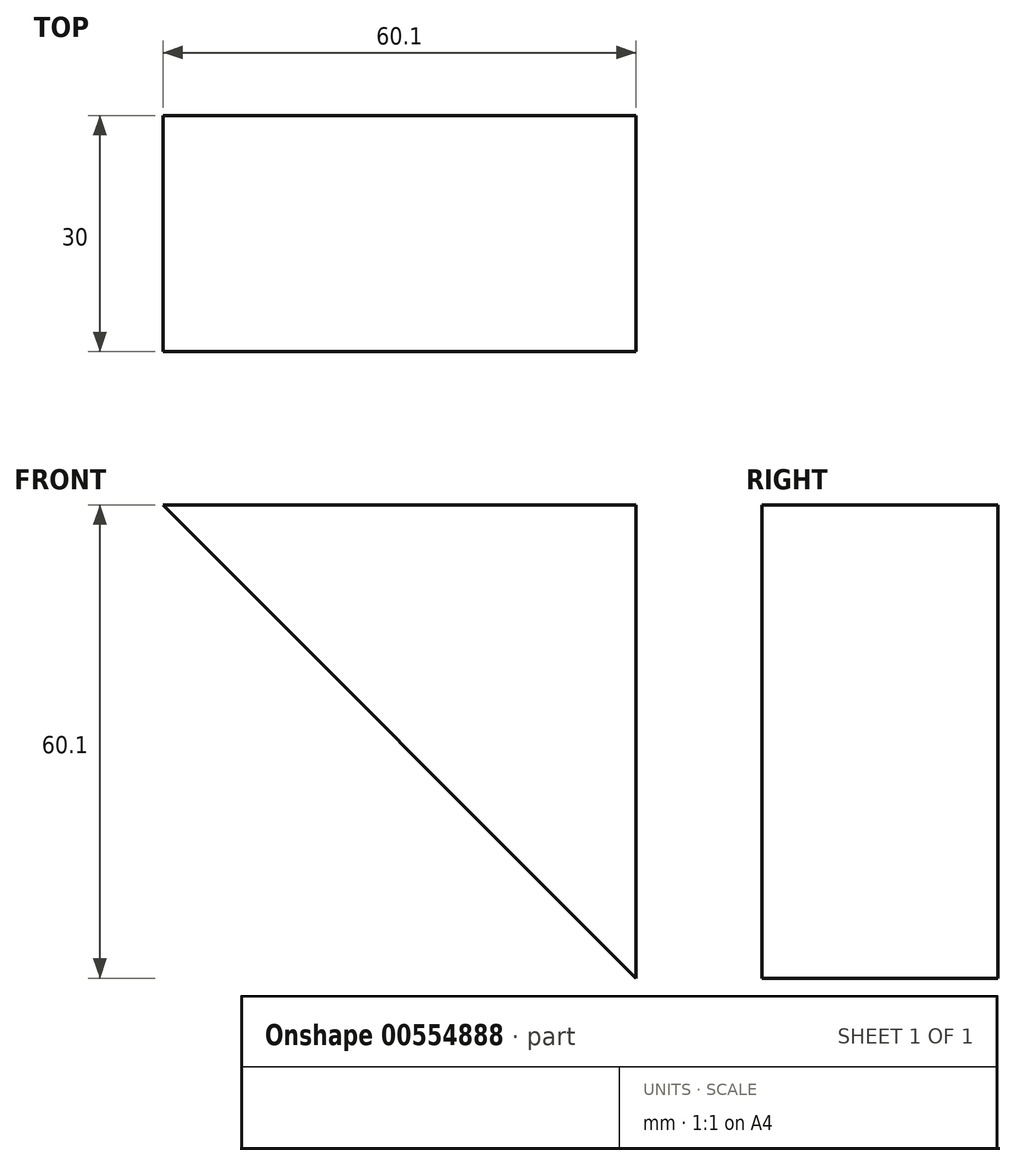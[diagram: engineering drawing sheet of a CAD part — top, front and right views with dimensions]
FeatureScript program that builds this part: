
annotation { "Feature Type Name" : "Feature", "Feature Type Description" : "" }
export const myFeature = defineFeature(function(context is Context, id is Id, definition is map)
    precondition{}
    {
        {
            var Q0;
            Q0=qCreatedBy(makeId("Front.planeOp"),FACE);
            var sketch = newSketch(context, id + "F0", { "sketchPlane" : qUnion([Q0])});
            skLineSegment(sketch, "E0", {"start": v(-119.33, 52.29) * mm, "end": v(-59.23, -7.81) * mm});
            skLineSegment(sketch, "E1", {"start": v(-59.23, -7.81) * mm, "end": v(-59.23, 52.29) * mm});
            skLineSegment(sketch, "E2", {"start": v(-59.23, 52.29) * mm, "end": v(-119.33, 52.29) * mm});
            skSolve(sketch);
        }
        {
            var Q0;
            Q0 = qSketchRegion(id + "F0", true);
            extrude(context, id + "F1", {"entities" : qUnion([Q0]), "depth" : 30 * mm, "offsetDistance" : 25 * mm});
        }
    });
